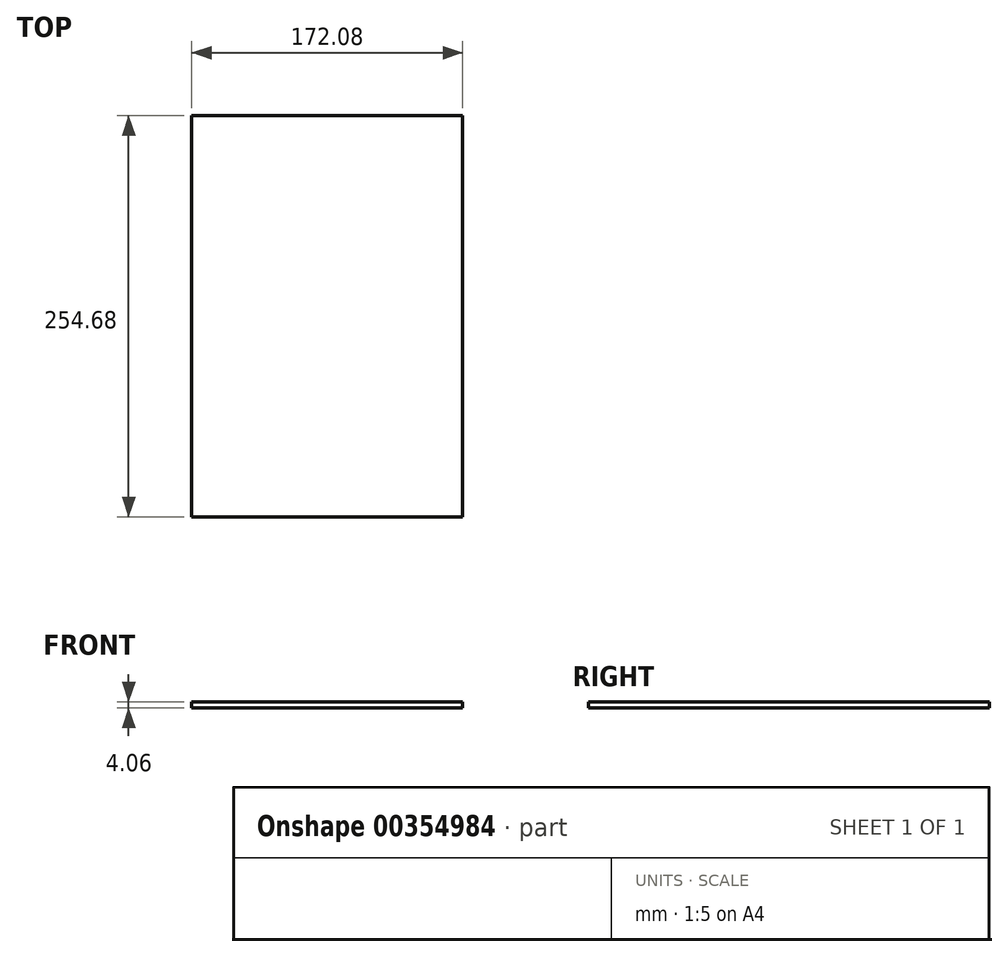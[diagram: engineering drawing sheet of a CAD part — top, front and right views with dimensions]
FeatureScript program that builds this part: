
annotation { "Feature Type Name" : "Feature", "Feature Type Description" : "" }
export const myFeature = defineFeature(function(context is Context, id is Id, definition is map)
    precondition{}
    {
        {
            var Q0;
            Q0=qCreatedBy(makeId("Top.planeOp"),FACE);
            var sketch = newSketch(context, id + "F0", { "sketchPlane" : qUnion([Q0])});
            skLineSegment(sketch, "E0.bottom", {"start": v(86.04, 127.34) * mm, "end": v(-86.04, 127.34) * mm});
            skLineSegment(sketch, "E0.top", {"start": v(86.04, -127.34) * mm, "end": v(-86.04, -127.34) * mm});
            skLineSegment(sketch, "E0.left", {"start": v(86.04, 127.34) * mm, "end": v(86.04, -127.34) * mm});
            skLineSegment(sketch, "E0.right", {"start": v(-86.04, 127.34) * mm, "end": v(-86.04, -127.34) * mm});
            skPoint(sketch, "E0.middle", {"position": v(0, 0) * mm});
            skSolve(sketch);
        }
        {
            var Q0;
            Q0 = qSketchRegion(id + "F0", true);
            extrude(context, id + "F1", {"entities" : qUnion([Q0]), "depth" : 4.06 * mm});
        }
    });
